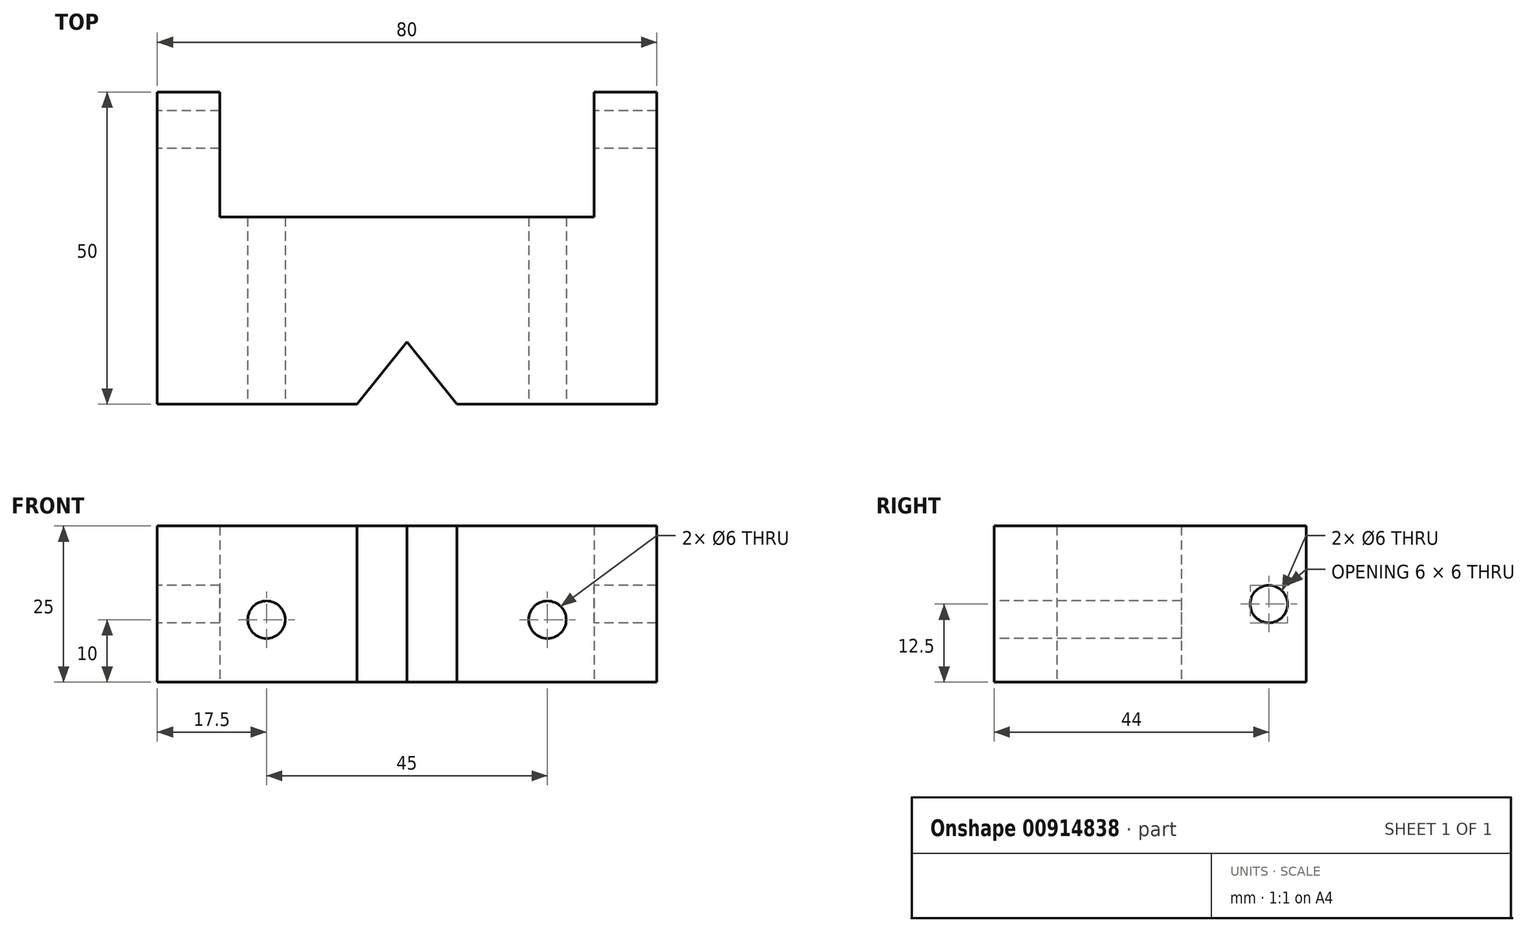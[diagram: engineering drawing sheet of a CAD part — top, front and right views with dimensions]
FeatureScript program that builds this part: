
annotation { "Feature Type Name" : "Feature", "Feature Type Description" : "" }
export const myFeature = defineFeature(function(context is Context, id is Id, definition is map)
    precondition{}
    {
        {
            var Q0;
            Q0=qCreatedBy(makeId("Top.planeOp"),FACE);
            var sketch = newSketch(context, id + "F0", { "sketchPlane" : qUnion([Q0])});
            skLineSegment(sketch, "E0.top", {"start": v(0, 50) * mm, "end": v(10, 50) * mm});
            skLineSegment(sketch, "E0.left", {"start": v(0, 0) * mm, "end": v(0, 50) * mm});
            skLineSegment(sketch, "E0.right", {"start": v(80, 0) * mm, "end": v(80, 50) * mm});
            skLineSegment(sketch, "E1.top", {"start": v(10, 30) * mm, "end": v(70, 30) * mm});
            skLineSegment(sketch, "E1.left", {"start": v(10, 50) * mm, "end": v(10, 30) * mm});
            skLineSegment(sketch, "E1.right", {"start": v(70, 50) * mm, "end": v(70, 30) * mm});
            skLineSegment(sketch, "E2.trimOffspring", {"start": v(70, 50) * mm, "end": v(80, 50) * mm});
            skPoint(sketch, "E3", {"position": v(40, 0) * mm});
            skLineSegment(sketch, "E4", {"start": v(40, 0) * mm, "end": v(40, 30) * mm, "construction": true});
            skLineSegment(sketch, "E5", {"start": v(32, 0) * mm, "end": v(40, 10) * mm});
            skLineSegment(sketch, "E6", {"start": v(40, 10) * mm, "end": v(48, 0) * mm});
            skLineSegment(sketch, "E7.trimOffspring", {"start": v(48, 0) * mm, "end": v(80, 0) * mm});
            skLineSegment(sketch, "E8", {"start": v(0, 0) * mm, "end": v(32, 0) * mm});
            skSolve(sketch);
        }
        {
            var Q0;
            Q0 = qSketchRegion(id + "F0", true);
            extrude(context, id + "F1", {"entities" : qUnion([Q0]), "depth" : 25 * mm, "offsetDistance" : 25 * mm});
        }
        {
            var Q0;
            Q0=makeQuery(id+"F1.opExtrude","SWEPT_FACE",FACE,{"disambiguationData":[OSD([sQuery(id+"F0.wireOp",EDGE,"E7.trimOffspring")])]});
            var sketch = newSketch(context, id + "F2", { "sketchPlane" : qUnion([Q0])});
            skCircle(sketch, "E9", {"center": v(17.5, 10) * mm, "radius": 3 * mm});
            skCircle(sketch, "E10", {"center": v(62.5, 10) * mm, "radius": 3 * mm});
            skSolve(sketch);
        }
        {
            var Q0;
            Q0 = qSketchRegion(id + "F2", true);
            extrude(context, id + "F3", {"entities" : qUnion([Q0]), "operationType" : NewBodyOperationType.REMOVE, "endBound" : BoundingType.THROUGH_ALL, "oppositeDirection" : true, "depth" : 25 * mm, "offsetDistance" : 25 * mm});
        }
        {
            var Q0;
            Q0=makeQuery(id+"F1.opExtrude","SWEPT_FACE",FACE,{"disambiguationData":[OSD([sQuery(id+"F0.wireOp",EDGE,"E0.left")])]});
            var sketch = newSketch(context, id + "F4", { "sketchPlane" : qUnion([Q0])});
            skCircle(sketch, "E11", {"center": v(-44, 12.5) * mm, "radius": 3 * mm});
            skSolve(sketch);
        }
        {
            var Q0;
            Q0 = qSketchRegion(id + "F4", true);
            extrude(context, id + "F5", {"entities" : qUnion([Q0]), "operationType" : NewBodyOperationType.REMOVE, "endBound" : BoundingType.THROUGH_ALL, "oppositeDirection" : true, "depth" : 25 * mm, "offsetDistance" : 25 * mm});
        }
    });
